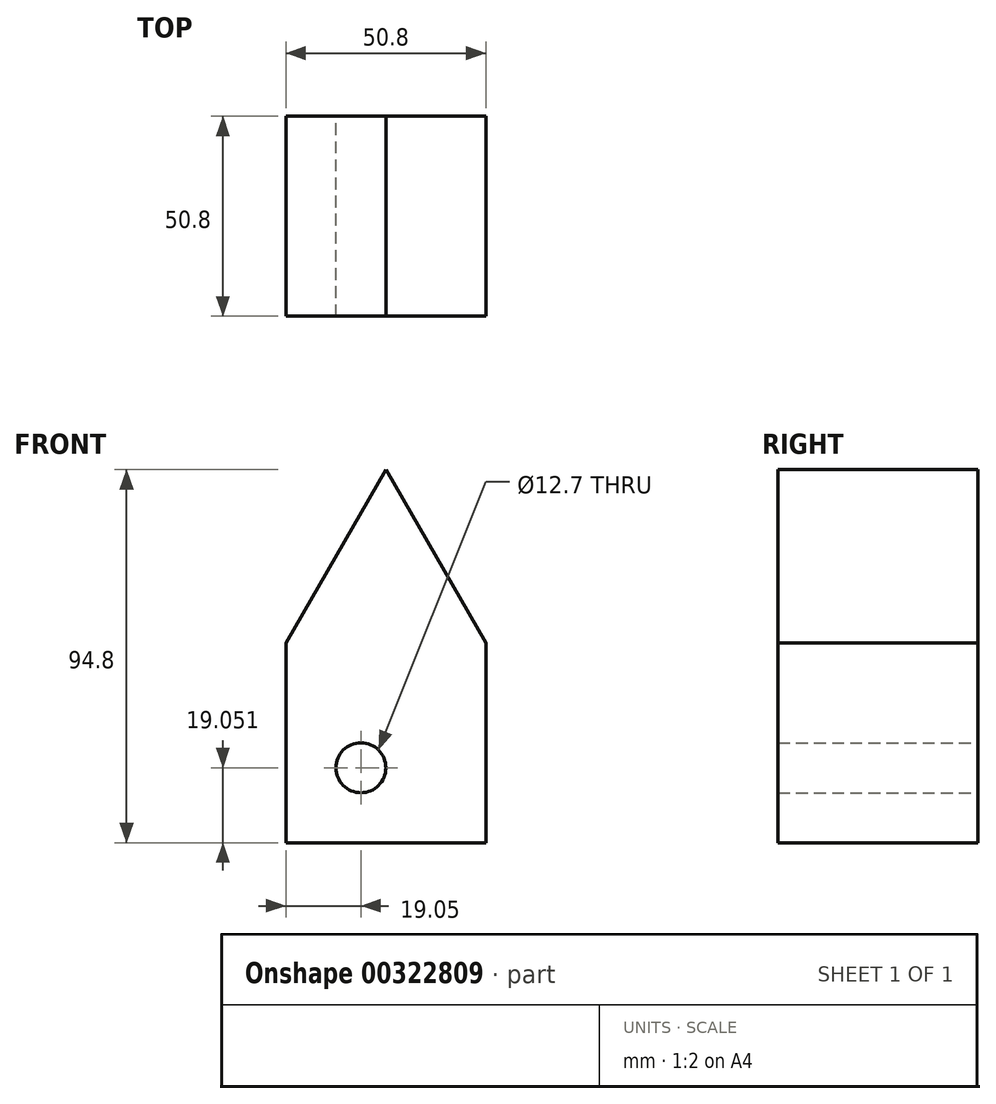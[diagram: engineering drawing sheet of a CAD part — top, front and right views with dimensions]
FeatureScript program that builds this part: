
annotation { "Feature Type Name" : "Feature", "Feature Type Description" : "" }
export const myFeature = defineFeature(function(context is Context, id is Id, definition is map)
    precondition{}
    {
        {
            var Q0;
            Q0=qCreatedBy(makeId("Front.planeOp"),FACE);
            var sketch = newSketch(context, id + "F0", { "sketchPlane" : qUnion([Q0])});
            skLineSegment(sketch, "E0.top", {"start": v(-25.4, -28.72) * mm, "end": v(25.4, -28.72) * mm});
            skLineSegment(sketch, "E0.left", {"start": v(-25.4, 22.08) * mm, "end": v(-25.4, -28.72) * mm});
            skLineSegment(sketch, "E0.right", {"start": v(25.4, 22.08) * mm, "end": v(25.4, -28.72) * mm});
            skLineSegment(sketch, "E1", {"start": v(-25.4, 22.08) * mm, "end": v(0, 66.08) * mm});
            skLineSegment(sketch, "E2", {"start": v(0, 66.08) * mm, "end": v(25.4, 22.08) * mm});
            skCircle(sketch, "E3", {"center": v(-6.35, -9.67) * mm, "radius": 6.35 * mm});
            skSolve(sketch);
        }
        {
            var Q0;
            Q0=makeQuery(id+"F0.imprint","IMPRINT",FACE,{"disambiguationData":[TD([[makeQuery(id+"F0.imprint","IMPRINT",EDGE,{"derivedFrom":sQuery(id+"F0.wireOp",EDGE,"E0.top")}),1.0]])]});
            extrude(context, id + "F1", {"entities" : qUnion([Q0]), "depth" : 50.8 * mm});
        }
    });
